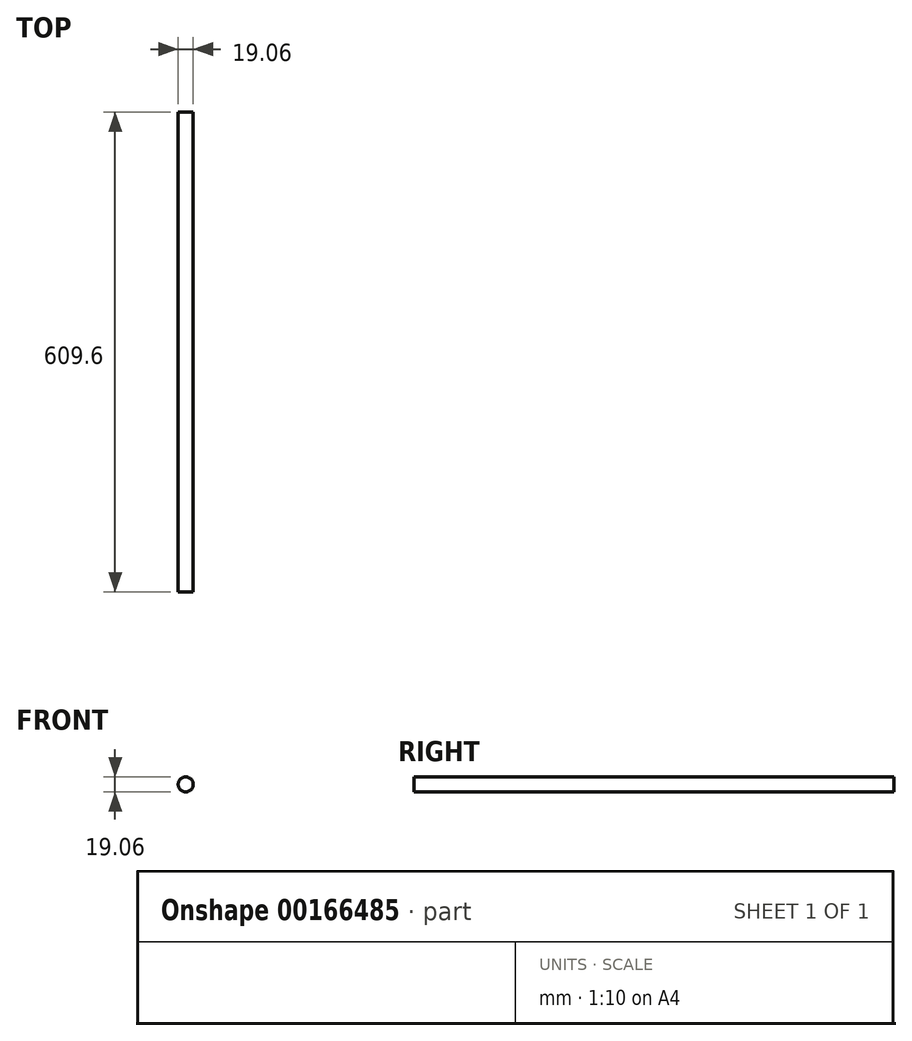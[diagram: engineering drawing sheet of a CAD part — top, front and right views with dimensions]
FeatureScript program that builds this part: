
annotation { "Feature Type Name" : "Feature", "Feature Type Description" : "" }
export const myFeature = defineFeature(function(context is Context, id is Id, definition is map)
    precondition{}
    {
        {
            var Q0;
            Q0=qCreatedBy(makeId("Front.planeOp"),FACE);
            var sketch = newSketch(context, id + "F0", { "sketchPlane" : qUnion([Q0])});
            skCircle(sketch, "E0", {"center": v(0, 0) * mm, "radius": 9.53 * mm});
            skSolve(sketch);
        }
        {
            var Q0;
            Q0 = qSketchRegion(id + "F0", true);
            extrude(context, id + "F1", {"entities" : qUnion([Q0]), "depth" : 609.6 * mm});
        }
    });
